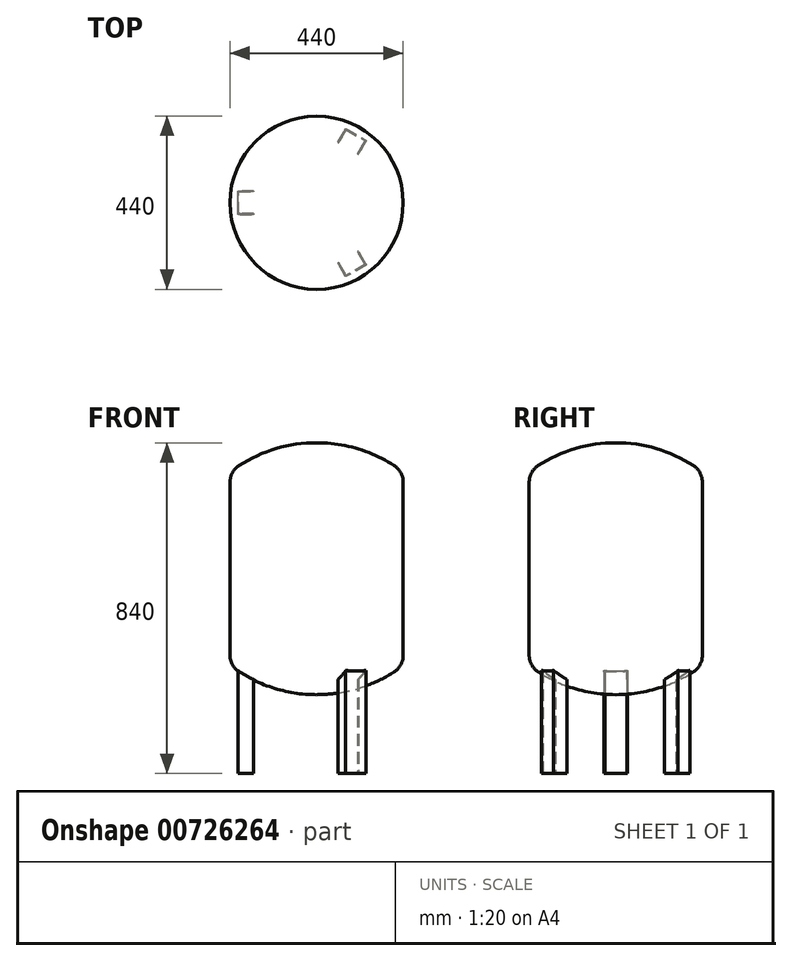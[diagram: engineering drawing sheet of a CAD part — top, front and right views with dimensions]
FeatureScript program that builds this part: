
annotation { "Feature Type Name" : "Feature", "Feature Type Description" : "" }
export const myFeature = defineFeature(function(context is Context, id is Id, definition is map)
    precondition{}
    {
        {
            var Q0;
            Q0=qCreatedBy(makeId("Front.planeOp"),FACE);
            var sketch = newSketch(context, id + "F0", { "sketchPlane" : qUnion([Q0])});
            skLineSegment(sketch, "E0", {"start": v(-220, 100) * mm, "end": v(-220, 540) * mm});
            skArc(sketch, "E1", {"start": v(0, 640) * mm, "mid": v(-102.7, 625.2) * mm, "end": v(-197.07, 582.04) * mm});
            skLineSegment(sketch, "E2", {"start": v(0, 640) * mm, "end": v(58.23, 640) * mm, "construction": true});
            skPoint(sketch, "E3.visualSharp", {"position": v(-220, 566) * mm});
            skArc(sketch, "E3.filletArc", {"start": v(-197.07, 582.04) * mm, "mid": v(-213.9, 563.94) * mm, "end": v(-220, 540) * mm});
            skArc(sketch, "E4", {"start": v(-197.07, 57.96) * mm, "mid": v(-102.7, 14.8) * mm, "end": v(0, 0) * mm});
            skPoint(sketch, "E5.visualSharp", {"position": v(-220, 74) * mm});
            skArc(sketch, "E5.filletArc", {"start": v(-220, 100) * mm, "mid": v(-213.9, 76.06) * mm, "end": v(-197.07, 57.96) * mm});
            skLineSegment(sketch, "E6", {"start": v(0, 0) * mm, "end": v(49.75, 0) * mm, "construction": true});
            skLineSegment(sketch, "E7", {"start": v(0, 640) * mm, "end": v(0, 0) * mm});
            skLineSegment(sketch, "E8", {"start": v(0, 640) * mm, "end": v(0, 722.44) * mm, "construction": true});
            skSolve(sketch);
        }
        {
            var Q0;
            Q0=makeQuery(id+"F0.imprint","IMPRINT",FACE,{"disambiguationData":[TD([[makeQuery(id+"F0.imprint","IMPRINT",EDGE,{"derivedFrom":sQuery(id+"F0.wireOp",EDGE,"E0")}),-1.0]])]});
            var Q1;
            Q1=sQuery(id+"F0.wireOp",EDGE,"E8");
            revolve(context, id + "F1", {"surfaceOperationType" : NewSurfaceOperationType.NEW, "entities" : qUnion([Q0]), "axis" : qUnion([Q1]), "revolveType" : RevolveType.FULL});
        }
        {
            var Q0;
            Q0=qCreatedBy(makeId("Top.planeOp"),FACE);
            var sketch = newSketch(context, id + "F2", { "sketchPlane" : qUnion([Q0])});
            skLineSegment(sketch, "E9", {"start": v(-160, -30) * mm, "end": v(-200, -30) * mm});
            skLineSegment(sketch, "E10", {"start": v(-200, -30) * mm, "end": v(-200, 30) * mm});
            skLineSegment(sketch, "E11", {"start": v(-200, 30) * mm, "end": v(-160, 30) * mm});
            skLineSegment(sketch, "E12", {"start": v(-200, 0) * mm, "end": v(0, 0) * mm, "construction": true});
            skLineSegment(sketch, "E13.0", {"start": v(-198, 28) * mm, "end": v(-160, 28) * mm});
            skLineSegment(sketch, "E13.1", {"start": v(-198, -28) * mm, "end": v(-198, 28) * mm});
            skLineSegment(sketch, "E13.2", {"start": v(-160, -28) * mm, "end": v(-198, -28) * mm});
            skLineSegment(sketch, "E14", {"start": v(-160, -28) * mm, "end": v(-160, -30) * mm});
            skLineSegment(sketch, "E15", {"start": v(-160, 30) * mm, "end": v(-160, 28) * mm});
            skLineSegment(sketch, "E16.1.0", {"start": v(104.25, -124.56) * mm, "end": v(123.25, -157.47) * mm});
            skLineSegment(sketch, "E16.1.1", {"start": v(123.25, -157.47) * mm, "end": v(74.75, -185.47) * mm});
            skLineSegment(sketch, "E16.1.2", {"start": v(74.75, -185.47) * mm, "end": v(55.75, -152.56) * mm});
            skLineSegment(sketch, "E16.1.3", {"start": v(125.98, -158.2) * mm, "end": v(74.02, -188.2) * mm});
            skLineSegment(sketch, "E16.1.4", {"start": v(74.02, -188.2) * mm, "end": v(54.02, -153.56) * mm});
            skLineSegment(sketch, "E16.1.5", {"start": v(105.98, -123.56) * mm, "end": v(125.98, -158.2) * mm});
            skLineSegment(sketch, "E16.1.6", {"start": v(54.02, -153.56) * mm, "end": v(55.75, -152.56) * mm});
            skLineSegment(sketch, "E16.1.7", {"start": v(104.25, -124.56) * mm, "end": v(105.98, -123.56) * mm});
            skLineSegment(sketch, "E16.2.0", {"start": v(55.75, 152.56) * mm, "end": v(74.75, 185.47) * mm});
            skLineSegment(sketch, "E16.2.1", {"start": v(74.75, 185.47) * mm, "end": v(123.25, 157.47) * mm});
            skLineSegment(sketch, "E16.2.2", {"start": v(123.25, 157.47) * mm, "end": v(104.25, 124.56) * mm});
            skLineSegment(sketch, "E16.2.3", {"start": v(74.02, 188.2) * mm, "end": v(125.98, 158.2) * mm});
            skLineSegment(sketch, "E16.2.4", {"start": v(125.98, 158.2) * mm, "end": v(105.98, 123.56) * mm});
            skLineSegment(sketch, "E16.2.5", {"start": v(54.02, 153.56) * mm, "end": v(74.02, 188.2) * mm});
            skLineSegment(sketch, "E16.2.6", {"start": v(105.98, 123.56) * mm, "end": v(104.25, 124.56) * mm});
            skLineSegment(sketch, "E16.2.7", {"start": v(55.75, 152.56) * mm, "end": v(54.02, 153.56) * mm});
            skPoint(sketch, "E16.center", {"position": v(0, 0) * mm});
            skSolve(sketch);
        }
        {
            var Q0;
            Q0 = qSketchRegion(id + "F2", true);
            var Q1;
            Q1=makeQuery(id+"F1.opRevolve","SWEPT_BODY",BODY,{"disambiguationData":[OSD([sQuery(id+"F0.wireOp",EDGE,"E0"),sQuery(id+"F0.wireOp",EDGE,"E1"),sQuery(id+"F0.wireOp",EDGE,"E3.filletArc"),sQuery(id+"F0.wireOp",EDGE,"E4"),sQuery(id+"F0.wireOp",EDGE,"E5.filletArc"),sQuery(id+"F0.wireOp",EDGE,"E7")])]});
            extrude(context, id + "F3", {"entities" : qUnion([Q0]), "operationType" : NewBodyOperationType.ADD, "endBound" : BoundingType.UP_TO_BODY, "depth" : 25 * mm, "endBoundEntityBody" : qUnion([Q1]), "offsetDistance" : 25 * mm, "hasSecondDirection" : true, "secondDirectionOppositeDirection" : true, "secondDirectionDepth" : 200 * mm});
        }
    });
